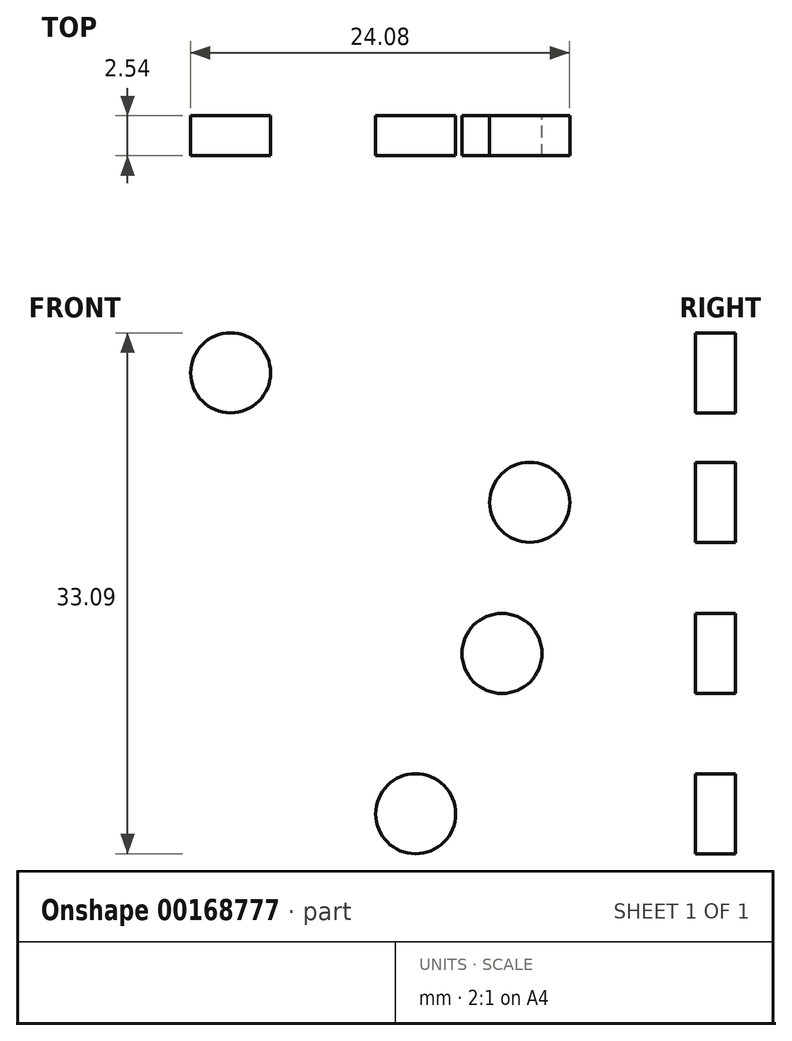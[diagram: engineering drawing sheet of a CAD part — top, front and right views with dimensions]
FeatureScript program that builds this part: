
annotation { "Feature Type Name" : "Feature", "Feature Type Description" : "" }
export const myFeature = defineFeature(function(context is Context, id is Id, definition is map)
    precondition{}
    {
        {
            var Q0;
            Q0=qCreatedBy(makeId("Front.planeOp"),FACE);
            var sketch = newSketch(context, id + "F0", { "sketchPlane" : qUnion([Q0])});
            skCircle(sketch, "E0", {"center": v(-52.69, 38.49) * mm, "radius": 2.54 * mm});
            skCircle(sketch, "E1", {"center": v(-33.69, 30.26) * mm, "radius": 2.54 * mm});
            skCircle(sketch, "E2", {"center": v(-35.45, 20.66) * mm, "radius": 2.54 * mm});
            skCircle(sketch, "E3", {"center": v(-40.94, 10.48) * mm, "radius": 2.54 * mm});
            skSolve(sketch);
        }
        {
            var Q0;
            Q0=makeQuery(id+"F0.imprint","IMPRINT",FACE,{"disambiguationData":[TD([[makeQuery(id+"F0.imprint","IMPRINT",EDGE,{"derivedFrom":sQuery(id+"F0.wireOp",EDGE,"E2")}),1.0]])]});
            var Q1;
            Q1=makeQuery(id+"F0.imprint","IMPRINT",FACE,{"disambiguationData":[TD([[makeQuery(id+"F0.imprint","IMPRINT",EDGE,{"derivedFrom":sQuery(id+"F0.wireOp",EDGE,"E1")}),1.0]])]});
            var Q2;
            Q2=makeQuery(id+"F0.imprint","IMPRINT",FACE,{"disambiguationData":[TD([[makeQuery(id+"F0.imprint","IMPRINT",EDGE,{"derivedFrom":sQuery(id+"F0.wireOp",EDGE,"E3")}),1.0]])]});
            var Q3;
            Q3=makeQuery(id+"F0.imprint","IMPRINT",FACE,{"disambiguationData":[TD([[makeQuery(id+"F0.imprint","IMPRINT",EDGE,{"derivedFrom":sQuery(id+"F0.wireOp",EDGE,"E0")}),1.0]])]});
            extrude(context, id + "F1", {"entities" : qUnion([Q0, Q1, Q2, Q3]), "endBound" : BoundingType.SYMMETRIC, "depth" : 2.54 * mm});
        }
    });
